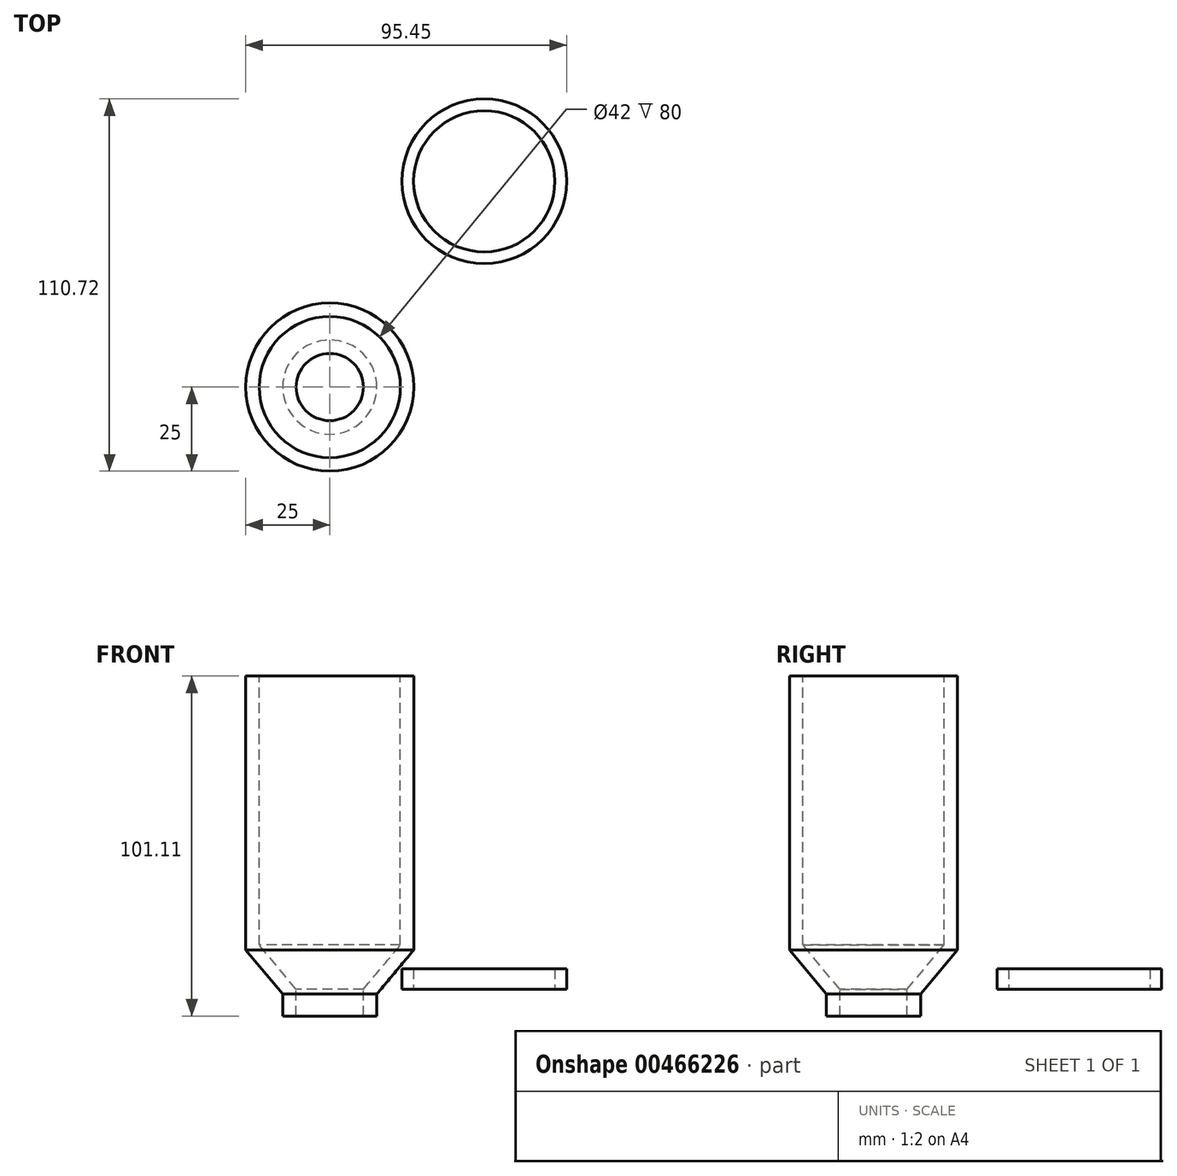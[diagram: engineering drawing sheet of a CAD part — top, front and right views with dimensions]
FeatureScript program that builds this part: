
annotation { "Feature Type Name" : "Feature", "Feature Type Description" : "" }
export const myFeature = defineFeature(function(context is Context, id is Id, definition is map)
    precondition{}
    {
        {
            var Q0;
            Q0=qCreatedBy(makeId("Front.planeOp"),FACE);
            var sketch = newSketch(context, id + "F0", { "sketchPlane" : qUnion([Q0])});
            skLineSegment(sketch, "E0", {"start": v(0, 0) * mm, "end": v(10, 0) * mm, "construction": true});
            skLineSegment(sketch, "E1", {"start": v(10, 0) * mm, "end": v(21, 13.1) * mm});
            skLineSegment(sketch, "E2", {"start": v(21, 13.1) * mm, "end": v(0, 13.1) * mm, "construction": true});
            skLineSegment(sketch, "E3", {"start": v(0, 13.1) * mm, "end": v(0, 0) * mm, "construction": true});
            skLineSegment(sketch, "E4", {"start": v(21, 13.1) * mm, "end": v(21, 93.1) * mm});
            skLineSegment(sketch, "E5", {"start": v(10, 0) * mm, "end": v(10, -8) * mm});
            skLineSegment(sketch, "E6", {"start": v(10, -8) * mm, "end": v(14, -8) * mm});
            skLineSegment(sketch, "E7", {"start": v(14, -8) * mm, "end": v(14, -1.46) * mm});
            skLineSegment(sketch, "E8", {"start": v(25, 13.1) * mm, "end": v(25, 93.1) * mm});
            skLineSegment(sketch, "E9", {"start": v(25, 93.1) * mm, "end": v(21, 93.1) * mm});
            skPoint(sketch, "E10.orphan", {"position": v(14, 3.1) * mm});
            skLineSegment(sketch, "E11", {"start": v(25, 13.1) * mm, "end": v(25, 11.65) * mm});
            skLineSegment(sketch, "E12", {"start": v(25, 11.65) * mm, "end": v(14, -1.46) * mm});
            skSolve(sketch);
        }
        {
            var Q0;
            Q0 = qSketchRegion(id + "F0", true);
            var Q1;
            Q1=sQuery(id+"F0.wireOp",EDGE,"E3");
            revolve(context, id + "F1", {"entities" : qUnion([Q0]), "axis" : qUnion([Q1]), "revolveType" : RevolveType.FULL});
        }
        {
            var Q0;
            Q0=qCreatedBy(makeId("Top.planeOp"),FACE);
            var sketch = newSketch(context, id + "F2", { "sketchPlane" : qUnion([Q0])});
            skCircle(sketch, "E13", {"center": v(45.95, 61.22) * mm, "radius": 21 * mm});
            skCircle(sketch, "E14", {"center": v(45.95, 61.22) * mm, "radius": 24.5 * mm});
            skSolve(sketch);
        }
        {
            var Q0;
            Q0 = qSketchRegion(id + "F2", true);
            extrude(context, id + "F3", {"entities" : qUnion([Q0]), "depth" : 6 * mm});
        }
    });
